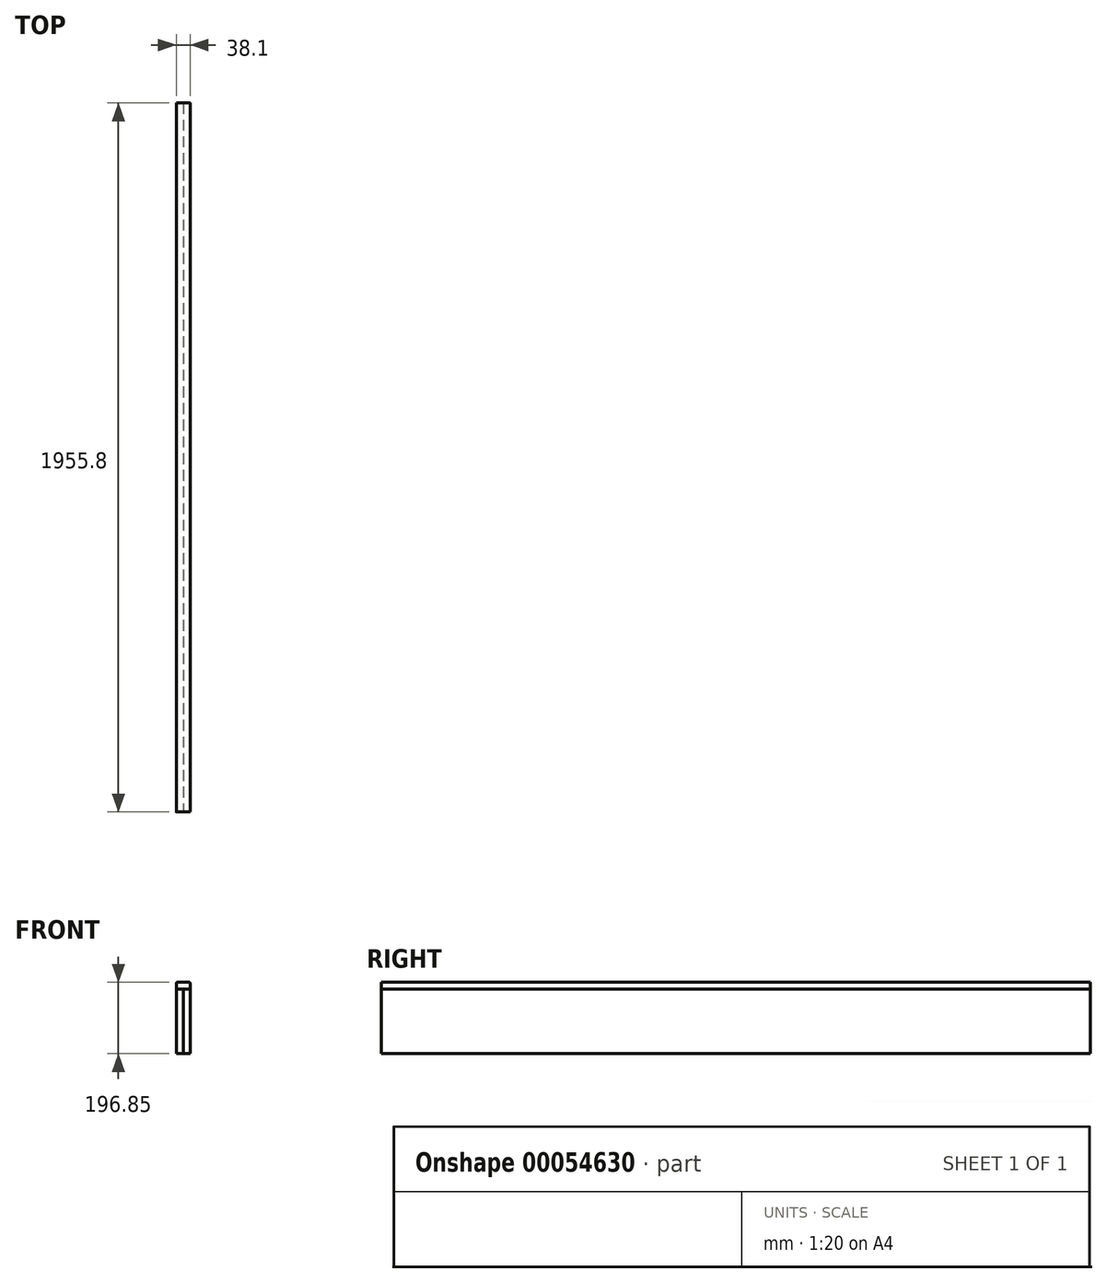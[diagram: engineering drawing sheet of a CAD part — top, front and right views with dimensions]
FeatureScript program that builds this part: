
annotation { "Feature Type Name" : "Feature", "Feature Type Description" : "" }
export const myFeature = defineFeature(function(context is Context, id is Id, definition is map)
    precondition{}
    {
        {
            var Q0;
            Q0=qCreatedBy(makeId("Right.planeOp"),FACE);
            var sketch = newSketch(context, id + "F0", { "sketchPlane" : qUnion([Q0])});
            skLineSegment(sketch, "E0.bottom", {"start": v(0, 0) * mm, "end": v(-1955.8, 0) * mm});
            skLineSegment(sketch, "E0.top", {"start": v(0, 177.8) * mm, "end": v(-1955.8, 177.8) * mm});
            skLineSegment(sketch, "E0.left", {"start": v(0, 0) * mm, "end": v(0, 177.8) * mm});
            skLineSegment(sketch, "E0.right", {"start": v(-1955.8, 0) * mm, "end": v(-1955.8, 177.8) * mm});
            skSolve(sketch);
        }
        {
            var Q0;
            Q0=makeQuery(id+"F0.imprint","IMPRINT",FACE,{"disambiguationData":[TD([[makeQuery(id+"F0.imprint","IMPRINT",EDGE,{"derivedFrom":sQuery(id+"F0.wireOp",EDGE,"E0.bottom")}),-1.0]])]});
            extrude(context, id + "F1", {"entities" : qUnion([Q0]), "depth" : 19.05 * mm});
        }
        {
            var Q0;
            Q0=makeQuery(id+"F1.opExtrude","CAP_FACE",FACE,{"disambiguationData":[OSD([sQuery(id+"F0.wireOp",EDGE,"E0.bottom"),sQuery(id+"F0.wireOp",EDGE,"E0.top"),sQuery(id+"F0.wireOp",EDGE,"E0.left"),sQuery(id+"F0.wireOp",EDGE,"E0.right")])],"isStart":false});
            var sketch = newSketch(context, id + "F2", { "sketchPlane" : qUnion([Q0])});
            skLineSegment(sketch, "E1.bottom", {"start": v(-1955.8, 177.8) * mm, "end": v(0, 177.8) * mm});
            skLineSegment(sketch, "E1.top", {"start": v(-1955.8, 0) * mm, "end": v(0, 0) * mm});
            skLineSegment(sketch, "E1.left", {"start": v(-1955.8, 177.8) * mm, "end": v(-1955.8, 0) * mm});
            skLineSegment(sketch, "E1.right", {"start": v(0, 177.8) * mm, "end": v(0, 0) * mm});
            skSolve(sketch);
        }
        {
            var Q0;
            Q0=makeQuery(id+"F2.imprint","IMPRINT",FACE,{"disambiguationData":[TD([[makeQuery(id+"F2.imprint","IMPRINT",EDGE,{"derivedFrom":sQuery(id+"F2.wireOp",EDGE,"E1.bottom")}),1.0]])]});
            extrude(context, id + "F3", {"entities" : qUnion([Q0]), "depth" : 19.05 * mm});
        }
        {
            var Q0;
            Q0=makeQuery(id+"F1.opExtrude","SWEPT_FACE",FACE,{"disambiguationData":[OSD([sQuery(id+"F0.wireOp",EDGE,"E0.right")])]});
            var sketch = newSketch(context, id + "F4", { "sketchPlane" : qUnion([Q0])});
            skLineSegment(sketch, "E2.bottom", {"start": v(0, 177.8) * mm, "end": v(38.1, 177.8) * mm});
            skLineSegment(sketch, "E2.top", {"start": v(0, 196.85) * mm, "end": v(38.1, 196.85) * mm});
            skLineSegment(sketch, "E2.left", {"start": v(0, 177.8) * mm, "end": v(0, 196.85) * mm});
            skLineSegment(sketch, "E2.right", {"start": v(38.1, 177.8) * mm, "end": v(38.1, 196.85) * mm});
            skLineSegment(sketch, "E3.bottom", {"start": v(0, 177.8) * mm, "end": v(0, 177.8) * mm});
            skLineSegment(sketch, "E3.top", {"start": v(0, 146.05) * mm, "end": v(0, 146.05) * mm});
            skLineSegment(sketch, "E3.left", {"start": v(0, 177.8) * mm, "end": v(0, 146.05) * mm});
            skLineSegment(sketch, "E3.right", {"start": v(0, 177.8) * mm, "end": v(0, 146.05) * mm});
            skLineSegment(sketch, "E4.bottom", {"start": v(0, 0) * mm, "end": v(0, 0) * mm});
            skLineSegment(sketch, "E4.top", {"start": v(0, 50.8) * mm, "end": v(0, 50.8) * mm});
            skLineSegment(sketch, "E4.left", {"start": v(0, 0) * mm, "end": v(0, 50.8) * mm});
            skLineSegment(sketch, "E4.right", {"start": v(0, 0) * mm, "end": v(0, 50.8) * mm});
            skSolve(sketch);
        }
        {
            var Q0;
            Q0=makeQuery(id+"F4.imprint","IMPRINT",FACE,{"disambiguationData":[TD([[makeQuery(id+"F4.imprint","IMPRINT",EDGE,{"derivedFrom":sQuery(id+"F4.wireOp",EDGE,"E2.top")}),-1.0]])]});
            var Q1;
            Q1=makeQuery(id+"F3.opExtrude","SWEPT_FACE",FACE,{"disambiguationData":[OSD([sQuery(id+"F2.wireOp",EDGE,"E1.right")])]});
            extrude(context, id + "F5", {"entities" : qUnion([Q0]), "endBound" : BoundingType.UP_TO_SURFACE, "oppositeDirection" : true, "endBoundEntityFace" : qUnion([Q1]), "depth" : 25.4 * mm});
        }
        {
            var Q0;
            Q0=makeQuery(id+"F5.opExtrude","SWEPT_EDGE",EDGE,{"disambiguationData":[OSD([sQuery(id+"F4.wireOp",EDGE,"E2.top"),sQuery(id+"F4.wireOp",EDGE,"E2.left")])]});
            var Q1;
            Q1=makeQuery(id+"F5.opExtrude","SWEPT_EDGE",EDGE,{"disambiguationData":[OSD([sQuery(id+"F4.wireOp",EDGE,"E2.top"),sQuery(id+"F4.wireOp",EDGE,"E2.right")])]});
            fillet(context, id + "F6", {"entities" : qUnion([Q0, Q1]), "radius" : 2.54 * mm, "tangentPropagation" : true, "allowEdgeOverflow" : false});
        }
    });
